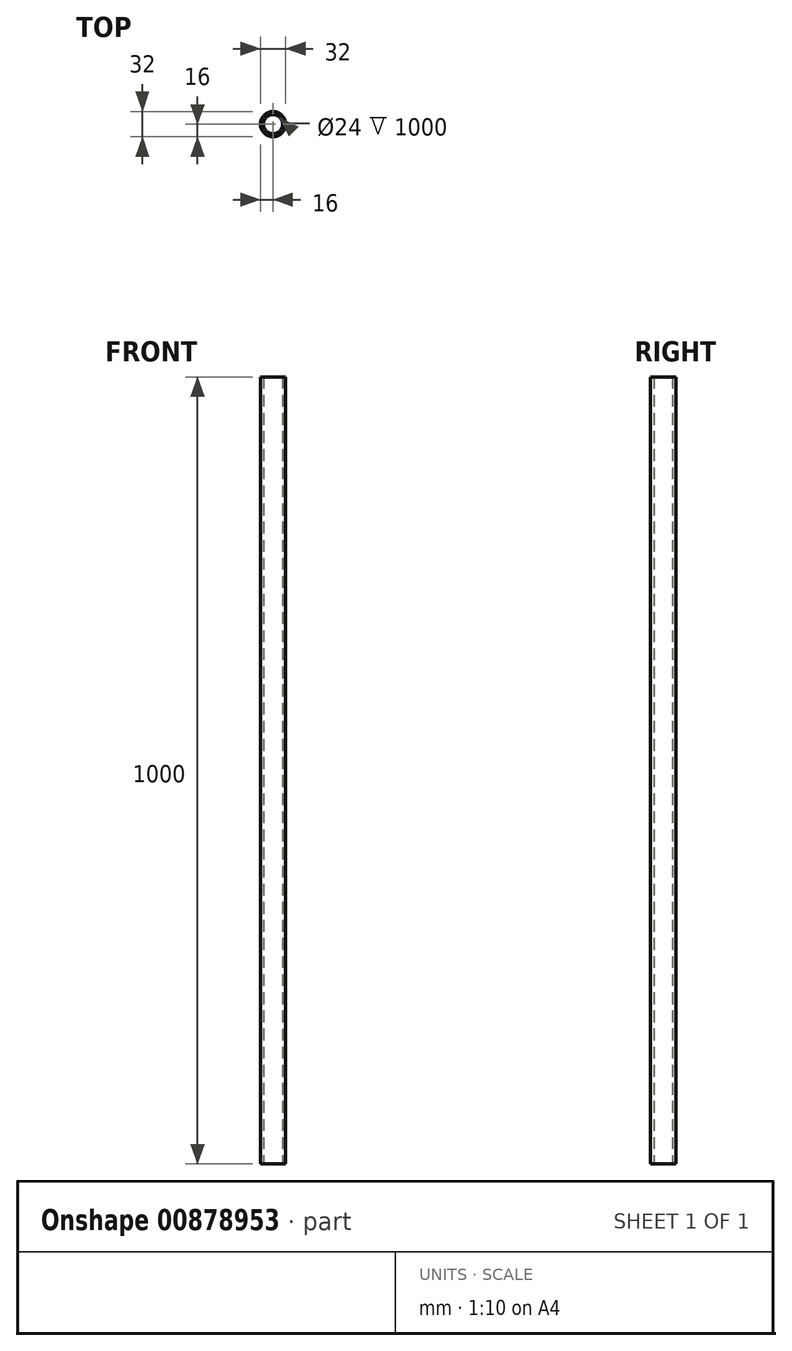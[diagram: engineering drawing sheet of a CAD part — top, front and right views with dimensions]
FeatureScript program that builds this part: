
annotation { "Feature Type Name" : "Feature", "Feature Type Description" : "" }
export const myFeature = defineFeature(function(context is Context, id is Id, definition is map)
    precondition{}
    {
        {
            var Q0;
            Q0=qCreatedBy(makeId("Top.planeOp"),FACE);
            var sketch = newSketch(context, id + "F0", { "sketchPlane" : qUnion([Q0])});
            skCircle(sketch, "E0", {"center": v(0, 0) * mm, "radius": 12 * mm});
            skCircle(sketch, "E1", {"center": v(0, 0) * mm, "radius": 16 * mm});
            skSolve(sketch);
        }
        {
            var Q0;
            Q0 = qSketchRegion(id + "F0", true);
            extrude(context, id + "F1", {"entities" : qUnion([Q0]), "depth" : 1000 * mm, "offsetDistance" : 25 * mm});
        }
    });
